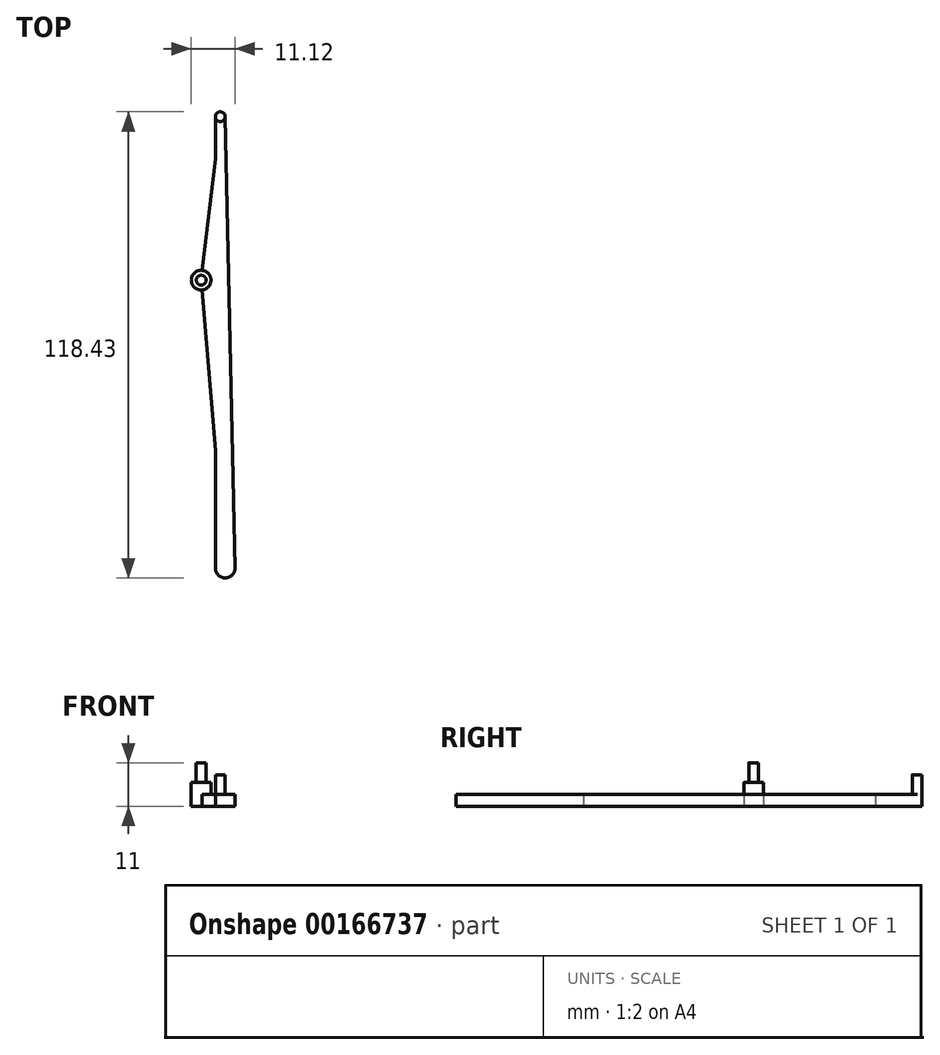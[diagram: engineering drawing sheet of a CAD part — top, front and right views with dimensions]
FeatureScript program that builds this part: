
annotation { "Feature Type Name" : "Feature", "Feature Type Description" : "" }
export const myFeature = defineFeature(function(context is Context, id is Id, definition is map)
    precondition{}
    {
        {
            var Q0;
            Q0=qCreatedBy(makeId("Top.planeOp"),FACE);
            var sketch = newSketch(context, id + "F0", { "sketchPlane" : qUnion([Q0])});
            skLineSegment(sketch, "E0", {"start": v(53.52, 83.94) * mm, "end": v(54.77, -30.74) * mm});
            skLineSegment(sketch, "E1", {"start": v(54.77, -30.74) * mm, "end": v(48.65, 42.41) * mm});
            skLineSegment(sketch, "E2", {"start": v(48.65, 42.41) * mm, "end": v(53.52, 83.94) * mm});
            skCircle(sketch, "E3", {"center": v(54.77, -30.74) * mm, "radius": 2.5 * mm});
            skCircle(sketch, "E4", {"center": v(53.52, 83.94) * mm, "radius": 1.25 * mm});
            skCircle(sketch, "E5", {"center": v(48.65, 42.41) * mm, "radius": 1.25 * mm});
            skCircle(sketch, "E6", {"center": v(48.65, 42.41) * mm, "radius": 2.5 * mm});
            skLineSegment(sketch, "E7", {"start": v(54.77, 83.97) * mm, "end": v(57.27, -30.68) * mm});
            skLineSegment(sketch, "E8", {"start": v(52.27, -30.74) * mm, "end": v(52.27, 83.94) * mm});
            skSolve(sketch);
        }
        {
            var Q0;
            {var subQ0=sQuery(id+"F0.wireOp",EDGE,"E6");var subQ1=sQuery(id+"F0.wireOp",EDGE,"E1");var subQ2=makeQuery(id+"F0.imprint","INTERSECT",VERTEX,{"derivedFrom":[subQ1,subQ0]});Q0=makeQuery(id+"F0.imprint","IMPRINT",FACE,{"disambiguationData":[TD([[makeQuery(id+"F0.imprint","IMPRINT",EDGE,{"disambiguationData":[TD([[subQ2,-1.0]])],"derivedFrom":subQ1}),1.0]])]});}
            var Q1;
            {var subQ0=sQuery(id+"F0.wireOp",EDGE,"E6");var subQ1=sQuery(id+"F0.wireOp",EDGE,"E1");var subQ2=makeQuery(id+"F0.imprint","INTERSECT",VERTEX,{"derivedFrom":[subQ1,subQ0]});Q1=makeQuery(id+"F0.imprint","IMPRINT",FACE,{"disambiguationData":[TD([[makeQuery(id+"F0.imprint","IMPRINT",EDGE,{"disambiguationData":[TD([[subQ2,-1.0]])],"derivedFrom":subQ1}),-1.0]])]});}
            extrude(context, id + "F1", {"entities" : qUnion([Q0, Q1]), "depth" : 6 * mm});
        }
        {
            var Q0;
            {var subQ0=sQuery(id+"F0.wireOp",EDGE,"E2");var subQ1=sQuery(id+"F0.wireOp",EDGE,"E1");var subQ2=makeQuery(id+"F0.imprint","INTERSECT",VERTEX,{"derivedFrom":[subQ1,subQ0]});Q0=makeQuery(id+"F0.imprint","IMPRINT",FACE,{"disambiguationData":[TD([[makeQuery(id+"F0.imprint","IMPRINT",EDGE,{"disambiguationData":[TD([[subQ2,1.0]])],"derivedFrom":subQ1}),-1.0]])]});}
            var Q1;
            {var subQ0=sQuery(id+"F0.wireOp",EDGE,"E2");var subQ1=sQuery(id+"F0.wireOp",EDGE,"E1");var subQ2=makeQuery(id+"F0.imprint","INTERSECT",VERTEX,{"derivedFrom":[subQ1,subQ0]});Q1=makeQuery(id+"F0.imprint","IMPRINT",FACE,{"disambiguationData":[TD([[makeQuery(id+"F0.imprint","IMPRINT",EDGE,{"disambiguationData":[TD([[subQ2,1.0]])],"derivedFrom":subQ1}),1.0]])]});}
            extrude(context, id + "F2", {"entities" : qUnion([Q0, Q1]), "depth" : 11 * mm});
        }
        {
            var Q0;
            {var subQ0=sQuery(id+"F0.wireOp",EDGE,"E2");var subQ1=sQuery(id+"F0.wireOp",EDGE,"E0");var subQ2=makeQuery(id+"F0.imprint","INTERSECT",VERTEX,{"derivedFrom":[subQ1,subQ0]});Q0=makeQuery(id+"F0.imprint","IMPRINT",FACE,{"disambiguationData":[TD([[makeQuery(id+"F0.imprint","IMPRINT",EDGE,{"disambiguationData":[TD([[subQ2,-1.0]])],"derivedFrom":subQ1}),-1.0]])]});}
            var Q1;
            {var subQ0=sQuery(id+"F0.wireOp",EDGE,"E2");var subQ1=sQuery(id+"F0.wireOp",EDGE,"E0");var subQ2=makeQuery(id+"F0.imprint","INTERSECT",VERTEX,{"derivedFrom":[subQ1,subQ0]});Q1=makeQuery(id+"F0.imprint","IMPRINT",FACE,{"disambiguationData":[TD([[makeQuery(id+"F0.imprint","IMPRINT",EDGE,{"disambiguationData":[TD([[subQ2,-1.0]])],"derivedFrom":subQ1}),1.0]])]});}
            extrude(context, id + "F3", {"entities" : qUnion([Q0, Q1]), "depth" : 8 * mm});
        }
        {
            var Q0;
            {var subQ1=sQuery(id+"F0.wireOp",EDGE,"E0");var subQ8=sQuery(id+"F0.wireOp",EDGE,"E4");var subQ11=makeQuery(id+"F0.imprint","INTERSECT",VERTEX,{"derivedFrom":[subQ1,subQ8]});Q0=makeQuery(id+"F0.imprint","IMPRINT",FACE,{"disambiguationData":[TD([[makeQuery(id+"F0.imprint","IMPRINT",EDGE,{"disambiguationData":[TD([[subQ11,-1.0]])],"derivedFrom":subQ1}),-1.0]])]});}
            var Q1;
            {var subQ0=sQuery(id+"F0.wireOp",EDGE,"E1");var subQ1=sQuery(id+"F0.wireOp",EDGE,"E0");var subQ2=makeQuery(id+"F0.imprint","INTERSECT",VERTEX,{"derivedFrom":[subQ1,subQ0]});Q1=makeQuery(id+"F0.imprint","IMPRINT",FACE,{"disambiguationData":[TD([[makeQuery(id+"F0.imprint","IMPRINT",EDGE,{"disambiguationData":[TD([[subQ2,1.0]])],"derivedFrom":subQ1}),-1.0]])]});}
            var Q2;
            {var subQ0=sQuery(id+"F0.wireOp",EDGE,"E1");var subQ1=sQuery(id+"F0.wireOp",EDGE,"E0");var subQ2=makeQuery(id+"F0.imprint","INTERSECT",VERTEX,{"derivedFrom":[subQ1,subQ0]});Q2=makeQuery(id+"F0.imprint","IMPRINT",FACE,{"disambiguationData":[TD([[makeQuery(id+"F0.imprint","IMPRINT",EDGE,{"disambiguationData":[TD([[subQ2,1.0]])],"derivedFrom":subQ1}),1.0]])]});}
            var Q3;
            {var subQ0=sQuery(id+"F0.wireOp",EDGE,"isxUdT54-d9z9-ehCl-5ULB-xYls7562Aj2D");var subQ1=sQuery(id+"F0.wireOp",EDGE,"E1");var subQ2=makeQuery(id+"F0.imprint","INTERSECT",VERTEX,{"derivedFrom":[subQ1,subQ0]});Q3=makeQuery(id+"F0.imprint","IMPRINT",FACE,{"disambiguationData":[TD([[makeQuery(id+"F0.imprint","IMPRINT",EDGE,{"disambiguationData":[TD([[subQ2,-1.0]])],"derivedFrom":subQ1}),-1.0]])]});}
            var Q4;
            {var subQ0=sQuery(id+"F0.wireOp",EDGE,"isxUdT54-d9z9-ehCl-5ULB-xYls7562Aj2D");var subQ1=sQuery(id+"F0.wireOp",EDGE,"E1");var subQ2=makeQuery(id+"F0.imprint","INTERSECT",VERTEX,{"derivedFrom":[subQ1,subQ0]});Q4=makeQuery(id+"F0.imprint","IMPRINT",FACE,{"disambiguationData":[TD([[makeQuery(id+"F0.imprint","IMPRINT",EDGE,{"disambiguationData":[TD([[subQ2,-1.0]])],"derivedFrom":subQ1}),1.0]])]});}
            var Q5;
            {var subQ5=sQuery(id+"F0.wireOp",EDGE,"E7");Q5=makeQuery(id+"F0.imprint","IMPRINT",FACE,{"disambiguationData":[TD([[makeQuery(id+"F0.imprint","IMPRINT",EDGE,{"derivedFrom":subQ5}),-1.0]])]});}
            var Q6;
            {var subQ0=sQuery(id+"F0.wireOp",EDGE,"E8");var subQ1=sQuery(id+"F0.wireOp",EDGE,"E1");var subQ2=makeQuery(id+"F0.imprint","INTERSECT",VERTEX,{"derivedFrom":[subQ1,subQ0]});Q6=makeQuery(id+"F0.imprint","IMPRINT",FACE,{"disambiguationData":[TD([[makeQuery(id+"F0.imprint","IMPRINT",EDGE,{"disambiguationData":[TD([[subQ2,-1.0]])],"derivedFrom":subQ1}),-1.0]])]});}
            var Q7;
            {var subQ0=sQuery(id+"F0.wireOp",EDGE,"E8");var subQ1=sQuery(id+"F0.wireOp",EDGE,"E2");var subQ2=makeQuery(id+"F0.imprint","INTERSECT",VERTEX,{"derivedFrom":[subQ1,subQ0]});Q7=makeQuery(id+"F0.imprint","IMPRINT",FACE,{"disambiguationData":[TD([[makeQuery(id+"F0.imprint","IMPRINT",EDGE,{"disambiguationData":[TD([[subQ2,-1.0]])],"derivedFrom":subQ1}),1.0]])]});}
            extrude(context, id + "F4", {"entities" : qUnion([Q0, Q1, Q2, Q3, Q4, Q5, Q6, Q7]), "operationType" : NewBodyOperationType.ADD, "depth" : 3 * mm});
        }
    });
